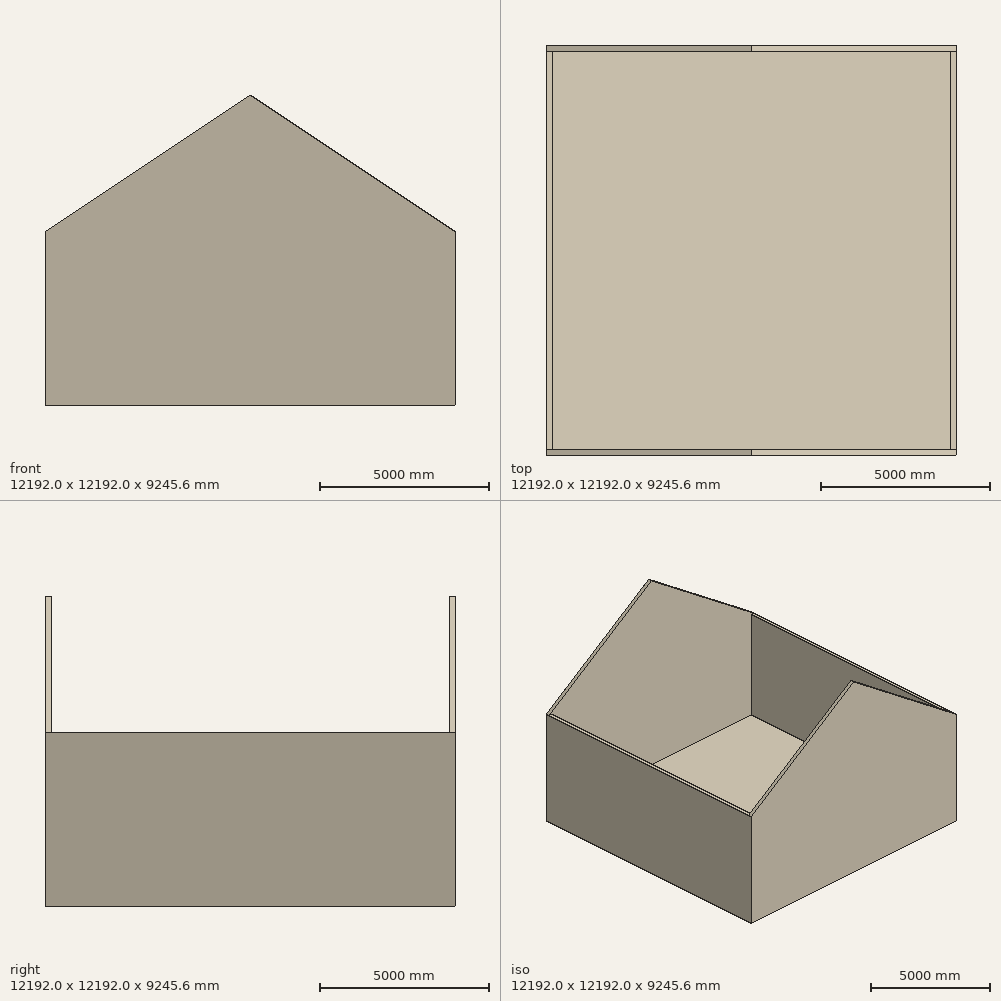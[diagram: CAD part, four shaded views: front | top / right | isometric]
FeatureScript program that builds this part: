
annotation { "Feature Type Name" : "Feature", "Feature Type Description" : "" }
export const myFeature = defineFeature(function(context is Context, id is Id, definition is map)
    precondition{}
    {
        {
            var Q0;
            Q0=qCreatedBy(makeId("Top.planeOp"),FACE);
            var sketch = newSketch(context, id + "F0", { "sketchPlane" : qUnion([Q0])});
            skLineSegment(sketch, "E0.bottom", {"start": v(0, 12192) * mm, "end": v(12192, 12192) * mm});
            skLineSegment(sketch, "E0.top", {"start": v(0, 0) * mm, "end": v(12192, 0) * mm});
            skLineSegment(sketch, "E0.left", {"start": v(0, 12192) * mm, "end": v(0, 0) * mm});
            skLineSegment(sketch, "E0.right", {"start": v(12192, 12192) * mm, "end": v(12192, 0) * mm});
            skSolve(sketch);
        }
        {
            var Q0;
            Q0=makeQuery(id+"F0.imprint","IMPRINT",FACE,{"disambiguationData":[TD([[makeQuery(id+"F0.imprint","IMPRINT",EDGE,{"derivedFrom":sQuery(id+"F0.wireOp",EDGE,"E0.bottom")}),-1.0]])]});
            extrude(context, id + "F1", {"entities" : qUnion([Q0]), "depth" : 304.8 * mm});
        }
        {
            var Q0;
            Q0=makeQuery(id+"F1.opExtrude","CAP_FACE",FACE,{"disambiguationData":[OSD([sQuery(id+"F0.wireOp",EDGE,"E0.bottom"),sQuery(id+"F0.wireOp",EDGE,"E0.top"),sQuery(id+"F0.wireOp",EDGE,"E0.left"),sQuery(id+"F0.wireOp",EDGE,"E0.right")])],"isStart":false});
            var sketch = newSketch(context, id + "F2", { "sketchPlane" : qUnion([Q0])});
            skLineSegment(sketch, "E1.0", {"start": v(0, 0) * mm, "end": v(12192, 0) * mm});
            skLineSegment(sketch, "E2.0", {"start": v(12192, 12192) * mm, "end": v(12192, 0) * mm});
            skLineSegment(sketch, "E3.0", {"start": v(0, 12192) * mm, "end": v(0, 0) * mm});
            skLineSegment(sketch, "E4.0", {"start": v(0, 12192) * mm, "end": v(12192, 12192) * mm});
            skLineSegment(sketch, "E5.0", {"start": v(165.1, 12026.9) * mm, "end": v(165.1, 165.1) * mm});
            skLineSegment(sketch, "E5.1", {"start": v(165.1, 12026.9) * mm, "end": v(12026.9, 12026.9) * mm});
            skLineSegment(sketch, "E5.2", {"start": v(12026.9, 12026.9) * mm, "end": v(12026.9, 165.1) * mm});
            skLineSegment(sketch, "E5.3", {"start": v(165.1, 165.1) * mm, "end": v(12026.9, 165.1) * mm});
            skSolve(sketch);
        }
        {
            var Q0;
            Q0=qSketchRegion(id+"F2",true);
            extrude(context, id + "F3", {"entities" : qUnion([Q0]), "operationType" : NewBodyOperationType.ADD, "depth" : 4876.8 * mm});
        }
        {
            var Q0;
            Q0=makeQuery(id+"F3.boolean.opBoolean","MERGE",FACE,{"derivedFrom":[makeQuery(id+"F1.opExtrude","SWEPT_FACE",FACE,{"disambiguationData":[OSD([sQuery(id+"F0.wireOp",EDGE,"E0.top")])]}),makeQuery(id+"F3.opExtrude","SWEPT_FACE",FACE,{"disambiguationData":[OSD([sQuery(id+"F2.wireOp",EDGE,"E1.0")])]})]});
            var sketch = newSketch(context, id + "F4", { "sketchPlane" : qUnion([Q0])});
            skLineSegment(sketch, "E6", {"start": v(0, 5181.6) * mm, "end": v(6096, 9245.6) * mm});
            skLineSegment(sketch, "E7", {"start": v(6096, 9245.6) * mm, "end": v(12192, 5181.6) * mm});
            skLineSegment(sketch, "E8", {"start": v(6096, 9245.6) * mm, "end": v(5791.2, 9245.6) * mm, "construction": true});
            skLineSegment(sketch, "E9", {"start": v(5791.2, 9245.6) * mm, "end": v(5791.2, 9042.4) * mm, "construction": true});
            skSolve(sketch);
        }
        {
            var Q0;
            Q0=makeQuery(id+"F4.imprint","IMPRINT",FACE,{"disambiguationData":[TD([[makeQuery(id+"F4.imprint","IMPRINT",EDGE,{"derivedFrom":sQuery(id+"F4.wireOp",EDGE,"E6")}),-1.0]])]});
            var Q1;
            Q1=makeQuery(id+"F3.opExtrude","SWEPT_FACE",FACE,{"disambiguationData":[OSD([sQuery(id+"F2.wireOp",EDGE,"E5.3")])]});
            extrude(context, id + "F5", {"entities" : qUnion([Q0]), "endBound" : BoundingType.UP_TO_SURFACE, "oppositeDirection" : true, "endBoundEntityFace" : qUnion([Q1]), "depth" : 25.4 * mm});
        }
        {
            var Q0;
            Q0=makeQuery(id+"F3.boolean.opBoolean","MERGE",FACE,{"derivedFrom":[makeQuery(id+"F1.opExtrude","SWEPT_FACE",FACE,{"disambiguationData":[OSD([sQuery(id+"F0.wireOp",EDGE,"E0.top")])]}),makeQuery(id+"F3.opExtrude","SWEPT_FACE",FACE,{"disambiguationData":[OSD([sQuery(id+"F2.wireOp",EDGE,"E1.0")])]})]});
            var Q1;
            Q1=makeQuery(id+"F3.boolean.opBoolean","MERGE",FACE,{"derivedFrom":[makeQuery(id+"F1.opExtrude","SWEPT_FACE",FACE,{"disambiguationData":[OSD([sQuery(id+"F0.wireOp",EDGE,"E0.bottom")])]}),makeQuery(id+"F3.opExtrude","SWEPT_FACE",FACE,{"disambiguationData":[OSD([sQuery(id+"F2.wireOp",EDGE,"E4.0")])]})]});
            cPlane(context, id + "F6", {"entities" : qUnion([Q0, Q1]), "cplaneType" : CPlaneType.MID_PLANE, "offset" : 152.4 * mm, "width" : 152.4 * mm, "height" : 152.4 * mm});
        }
        {
            var Q0;
            Q0=makeQuery(id+"F5.opExtrude","SWEPT_BODY",BODY,{"disambiguationData":[OSD([sQuery(id+"F2.wireOp",EDGE,"E1.0"),sQuery(id+"F4.wireOp",EDGE,"E6"),sQuery(id+"F4.wireOp",EDGE,"E7")])]});
            var Q1;
            Q1=qCreatedBy(id+"F6.planeOp",FACE);
            mirror(context, id + "F7", {"operationType" : NewBodyOperationType.ADD, "entities" : qUnion([Q0]), "mirrorPlane" : qUnion([Q1])});
        }
    });
